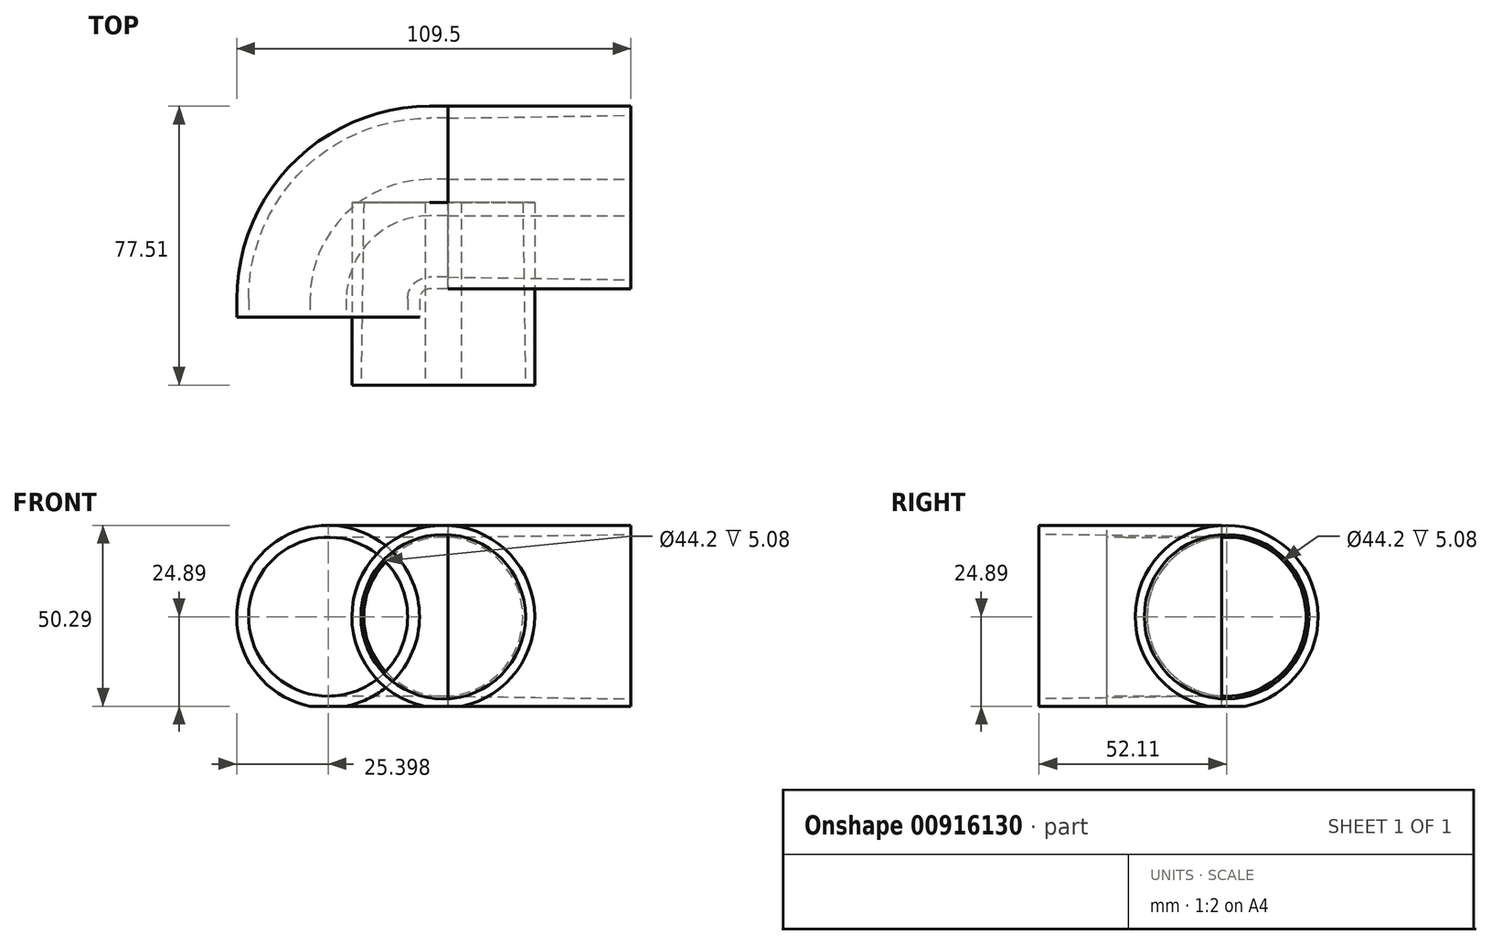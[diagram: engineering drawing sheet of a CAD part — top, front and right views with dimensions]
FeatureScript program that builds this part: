
annotation { "Feature Type Name" : "Feature", "Feature Type Description" : "" }
export const myFeature = defineFeature(function(context is Context, id is Id, definition is map)
    precondition{}
    {
        {
            assignVariable(context, id + "F0", {"name" : "OD", "anyValue" : 2});
        }
        {
            var Q0;
            Q0=qCreatedBy(makeId("Front.planeOp"),FACE);
            var sketch = newSketch(context, id + "F1", { "sketchPlane" : qUnion([Q0])});
            skLineSegment(sketch, "E0", {"start": v(0, 0) * mm, "end": v(-103.9, 0) * mm, "construction": true});
            skLineSegment(sketch, "E1", {"start": v(0, 25.4) * mm, "end": v(0, 22.1) * mm});
            skLineSegment(sketch, "E2", {"start": v(0, 22.1) * mm, "end": v(50.8, 22.86) * mm});
            skLineSegment(sketch, "E3", {"start": v(50.8, 22.86) * mm, "end": v(50.8, 25.4) * mm});
            skLineSegment(sketch, "E4", {"start": v(50.8, 25.4) * mm, "end": v(0, 25.4) * mm});
            skPoint(sketch, "E5", {"position": v(25.4, 22.48) * mm});
            skSolve(sketch);
        }
        {
            var Q0;
            Q0=qSketchRegion(id+"F1",true);
            var Q1;
            Q1=sQuery(id+"F1.wireOp",EDGE,"E0");
            revolve(context, id + "F2", {"surfaceOperationType" : NewSurfaceOperationType.NEW, "entities" : qUnion([Q0]), "axis" : qUnion([Q1]), "revolveType" : RevolveType.FULL});
        }
        {
            var Q0;
            Q0=qCreatedBy(makeId("Right.planeOp"),FACE);
            cPlane(context, id + "F3", {"entities" : qUnion([Q0]), "cplaneType" : CPlaneType.OFFSET, "offset" : ((getVariable(context, 'OD') / 1.8) + (getVariable(context, 'OD') / 10)) * mm, "oppositeDirection" : true, "width" : 152.4 * mm, "height" : 152.4 * mm});
        }
        {
            var Q0;
            Q0=qCreatedBy(id+"F3.planeOp",FACE);
            var sketch = newSketch(context, id + "F4", { "sketchPlane" : qUnion([Q0])});
            skLineSegment(sketch, "E6", {"start": v(0, 0) * mm, "end": v(0, 10.77) * mm, "construction": true});
            skSolve(sketch);
        }
        {
            var Q0;
            Q0=makeQuery(id+"F2.opRevolve","SWEPT_BODY",BODY,{"disambiguationData":[OSD([sQuery(id+"F1.wireOp",EDGE,"E1"),sQuery(id+"F1.wireOp",EDGE,"E2"),sQuery(id+"F1.wireOp",EDGE,"E3"),sQuery(id+"F1.wireOp",EDGE,"E4")])]});
            var Q1;
            Q1=sQuery(id+"F4.wireOp",EDGE,"E6");
            circularPattern(context, id + "F5", {"entities" : qUnion([Q0]), "axis" : qUnion([Q1]), "angle" : 90 * degree, "instanceCount" : 2, "oppositeDirection" : true, "equalSpace" : true});
        }
        {
            var Q0;
            Q0=qCreatedBy(makeId("Top.planeOp"),FACE);
            var sketch = newSketch(context, id + "F6", { "sketchPlane" : qUnion([Q0])});
            skLineSegment(sketch, "E7", {"start": v(0, 0) * mm, "end": v(-5.08, 0) * mm});
            skLineSegment(sketch, "E8", {"start": v(-33.3, -28.22) * mm, "end": v(-33.3, -33.3) * mm});
            skPoint(sketch, "E9.visualSharp", {"position": v(-33.3, 0) * mm});
            skArc(sketch, "E9.filletArc", {"start": v(-5.08, 0) * mm, "mid": v(-25.04, -8.27) * mm, "end": v(-33.3, -28.22) * mm});
            skSolve(sketch);
        }
        {
            var Q0;
            Q0=makeQuery(id+"F2.opRevolve","SWEPT_FACE",FACE,{"disambiguationData":[OSD([sQuery(id+"F1.wireOp",EDGE,"E1")])]});
            var Q1;
            Q1=qConstructionFilter(qBodyType(qCreatedBy(id+"F6",EDGE),BodyType.WIRE),ConstructionObject.NO);
            sweep(context, id + "F7", {"profiles" : qUnion([Q0]), "path" : qUnion([Q1])});
        }
        {
            var Q0;
            Q0=qCreatedBy(makeId("Right.planeOp"),FACE);
            var sketch = newSketch(context, id + "F8", { "sketchPlane" : qUnion([Q0])});
            skLineSegment(sketch, "E10.bottom", {"start": v(-101.6, -24.9) * mm, "end": v(25.4, -24.9) * mm});
            skLineSegment(sketch, "E10.top", {"start": v(-101.6, -25.4) * mm, "end": v(25.4, -25.4) * mm});
            skLineSegment(sketch, "E10.left", {"start": v(-101.6, -25.4) * mm, "end": v(-101.6, -24.9) * mm});
            skLineSegment(sketch, "E10.right", {"start": v(25.4, -25.4) * mm, "end": v(25.4, -24.9) * mm});
            skSolve(sketch);
        }
        {
            var Q0;
            Q0=qSketchRegion(id+"F8",true);
            extrude(context, id + "F9", {"entities" : qUnion([Q0]), "operationType" : NewBodyOperationType.REMOVE, "endBound" : BoundingType.THROUGH_ALL, "oppositeDirection" : true, "depth" : 25.4 * mm, "offsetDistance" : 25.4 * mm, "hasSecondDirection" : true, "secondDirectionBound" : SecondDirectionBoundingType.THROUGH_ALL, "secondDirectionOppositeDirection" : false, "secondDirectionDepth" : 25.4 * mm});
        }
    });
